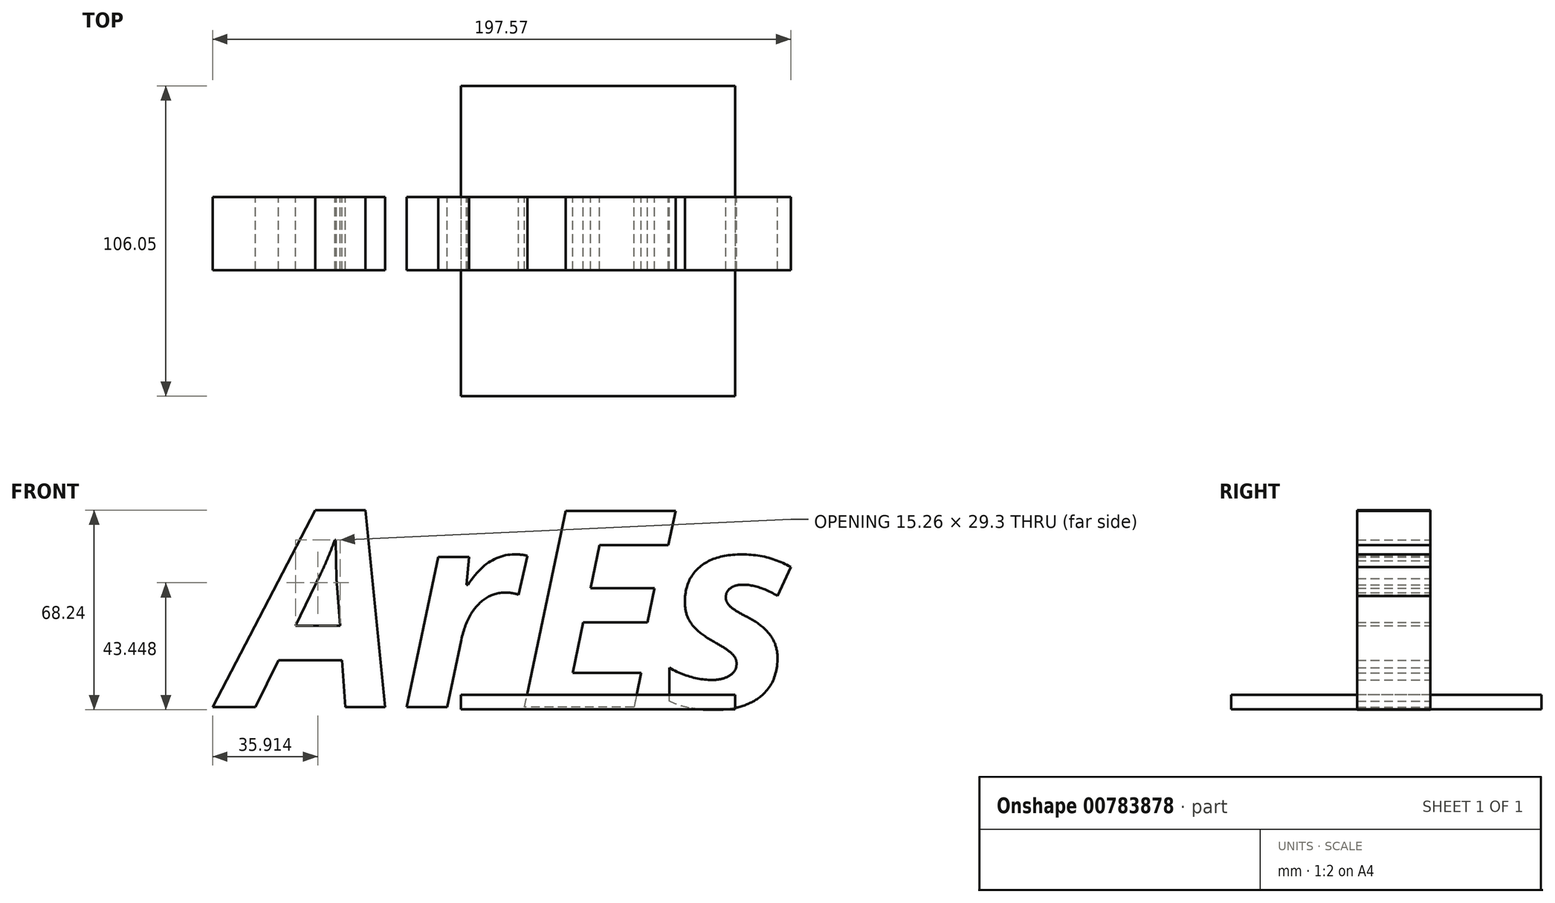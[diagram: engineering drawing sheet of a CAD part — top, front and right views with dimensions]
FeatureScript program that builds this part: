
annotation { "Feature Type Name" : "Feature", "Feature Type Description" : "" }
export const myFeature = defineFeature(function(context is Context, id is Id, definition is map)
    precondition{}
    {
        {
            var Q0;
            Q0=qCreatedBy(makeId("Front.planeOp"),FACE);
            var sketch = newSketch(context, id + "F0", { "sketchPlane" : qUnion([Q0])});
            skText(sketch, "E0", { "text": "ArEs", "fontName": "NotoSans-BoldItalic.ttf"});
            const initialGuessF0  = {"E0": [-0.12145, 0.00074, 1, 0, 0.06761]};
            skSetInitialGuess(sketch, initialGuessF0);
            skSolve(sketch);
        }
        {
            var Q0;
            Q0 = qSketchRegion(id + "F0", true);
            extrude(context, id + "F1", {"entities" : qUnion([Q0]), "depth" : 25 * mm, "offsetDistance" : 25 * mm});
        }
        {
            var Q0;
            Q0=qCreatedBy(makeId("Top.planeOp"),FACE);
            var sketch = newSketch(context, id + "F2", { "sketchPlane" : qUnion([Q0])});
            skLineSegment(sketch, "E1.bottom", {"start": v(-42.18, 37.94) * mm, "end": v(51.44, 37.94) * mm});
            skLineSegment(sketch, "E1.top", {"start": v(-42.18, -68.1) * mm, "end": v(51.44, -68.1) * mm});
            skLineSegment(sketch, "E1.left", {"start": v(-42.18, 37.94) * mm, "end": v(-42.18, -68.1) * mm});
            skLineSegment(sketch, "E1.right", {"start": v(51.44, 37.94) * mm, "end": v(51.44, -68.1) * mm});
            skSolve(sketch);
        }
        {
            var Q0;
            Q0 = qSketchRegion(id + "F2", true);
            extrude(context, id + "F3", {"entities" : qUnion([Q0]), "depth" : 5 * mm, "offsetDistance" : 25 * mm});
        }
    });
